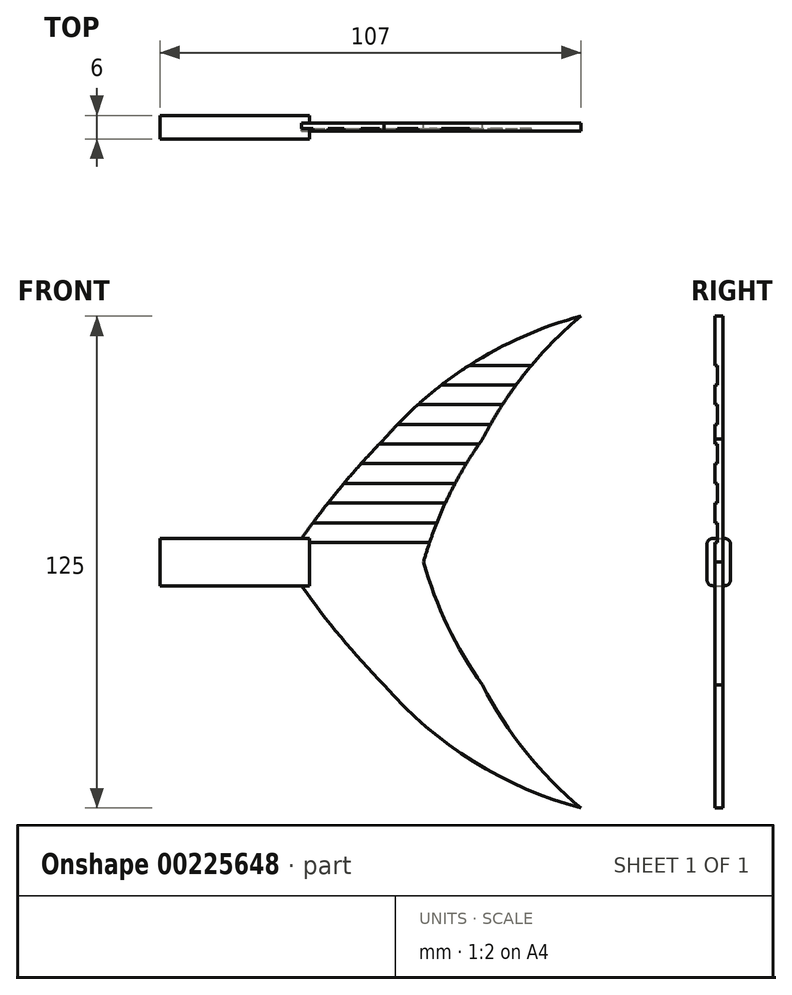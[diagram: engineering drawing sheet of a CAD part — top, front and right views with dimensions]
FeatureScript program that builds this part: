
annotation { "Feature Type Name" : "Feature", "Feature Type Description" : "" }
export const myFeature = defineFeature(function(context is Context, id is Id, definition is map)
    precondition{}
    {
        {
            var Q0;
            Q0=qCreatedBy(makeId("Front.planeOp"),FACE);
            var sketch = newSketch(context, id + "F0", { "sketchPlane" : qUnion([Q0])});
            skLineSegment(sketch, "E0", {"start": v(0, 0) * mm, "end": v(35, 0) * mm});
            skLineSegment(sketch, "E1", {"start": v(25, 31.25) * mm, "end": v(50, 31.25) * mm});
            skPoint(sketch, "E2", {"position": v(75, 62.5) * mm});
            skArc(sketch, "E3", {"start": v(25, 31.25) * mm, "mid": v(11.72, 16.25) * mm, "end": v(0, 0) * mm});
            skArc(sketch, "E4", {"start": v(75, 62.5) * mm, "mid": v(47.64, 50.64) * mm, "end": v(25, 31.25) * mm});
            skArc(sketch, "E5", {"start": v(75, 62.5) * mm, "mid": v(60.92, 48.14) * mm, "end": v(50, 31.25) * mm});
            skArc(sketch, "E6", {"start": v(50, 31.25) * mm, "mid": v(41.14, 16.28) * mm, "end": v(35, 0) * mm});
            skSolve(sketch);
        }
        {
            var Q0;
            Q0=qSketchRegion(id+"F0",true);
            extrude(context, id + "F1", {"entities" : qUnion([Q0]), "endBound" : BoundingType.SYMMETRIC, "depth" : 2 * mm});
        }
        {
            var Q0;
            Q0=makeQuery(id+"F1.opExtrude","SWEPT_BODY",BODY,{"disambiguationData":[OSD([sQuery(id+"F0.wireOp",EDGE,"E0"),sQuery(id+"F0.wireOp",EDGE,"E3"),sQuery(id+"F0.wireOp",EDGE,"E4"),sQuery(id+"F0.wireOp",EDGE,"E5"),sQuery(id+"F0.wireOp",EDGE,"E6")])]});
            var Q1;
            Q1=qCreatedBy(makeId("Top.planeOp"),FACE);
            mirror(context, id + "F2", {"operationType" : NewBodyOperationType.ADD, "entities" : qUnion([Q0]), "mirrorPlane" : qUnion([Q1])});
        }
        {
            var Q0;
            {var subQ0=makeQuery(id+"F1.opExtrude","CAP_FACE",FACE,{"disambiguationData":[OSD([sQuery(id+"F0.wireOp",EDGE,"E0"),sQuery(id+"F0.wireOp",EDGE,"E3"),sQuery(id+"F0.wireOp",EDGE,"E4"),sQuery(id+"F0.wireOp",EDGE,"E5"),sQuery(id+"F0.wireOp",EDGE,"E6")])],"isStart":false});Q0=makeQuery(id+"F2.boolean.opBoolean","MERGE",FACE,{"derivedFrom":[subQ0,makeQuery(id+"F2.opPattern","COPY",FACE,{"derivedFrom":subQ0,"instanceName":"1"})]});}
            var sketch = newSketch(context, id + "F3", { "sketchPlane" : qUnion([Q0])});
            skLineSegment(sketch, "E7.bottom", {"start": v(-1.98, 10) * mm, "end": v(47.03, 10) * mm});
            skLineSegment(sketch, "E7.top", {"start": v(-1.98, 5) * mm, "end": v(47.03, 5) * mm});
            skLineSegment(sketch, "E7.left", {"start": v(-1.98, 10) * mm, "end": v(-1.98, 5) * mm});
            skLineSegment(sketch, "E7.right", {"start": v(47.03, 10) * mm, "end": v(47.03, 5) * mm});
            skLineSegment(sketch, "E8.bottom", {"start": v(3.2, 20) * mm, "end": v(51.44, 20) * mm});
            skLineSegment(sketch, "E8.top", {"start": v(3.2, 15) * mm, "end": v(51.44, 15) * mm});
            skLineSegment(sketch, "E8.left", {"start": v(3.2, 20) * mm, "end": v(3.2, 15) * mm});
            skLineSegment(sketch, "E8.right", {"start": v(51.44, 20) * mm, "end": v(51.44, 15) * mm});
            skLineSegment(sketch, "E9.bottom", {"start": v(15.73, 30) * mm, "end": v(55.62, 30) * mm});
            skLineSegment(sketch, "E9.top", {"start": v(15.73, 25) * mm, "end": v(55.62, 25) * mm});
            skLineSegment(sketch, "E9.left", {"start": v(15.73, 30) * mm, "end": v(15.73, 25) * mm});
            skLineSegment(sketch, "E9.right", {"start": v(55.62, 30) * mm, "end": v(55.62, 25) * mm});
            skLineSegment(sketch, "E10.bottom", {"start": v(22.08, 40) * mm, "end": v(60.93, 40) * mm});
            skLineSegment(sketch, "E10.top", {"start": v(22.08, 35) * mm, "end": v(60.93, 35) * mm});
            skLineSegment(sketch, "E10.left", {"start": v(22.08, 40) * mm, "end": v(22.08, 35) * mm});
            skLineSegment(sketch, "E10.right", {"start": v(60.93, 40) * mm, "end": v(60.93, 35) * mm});
            skLineSegment(sketch, "E11.bottom", {"start": v(28.82, 50) * mm, "end": v(67.6, 50) * mm});
            skLineSegment(sketch, "E11.top", {"start": v(28.82, 45) * mm, "end": v(67.6, 45) * mm});
            skLineSegment(sketch, "E11.left", {"start": v(28.82, 50) * mm, "end": v(28.82, 45) * mm});
            skLineSegment(sketch, "E11.right", {"start": v(67.6, 50) * mm, "end": v(67.6, 45) * mm});
            skSolve(sketch);
        }
        {
            var Q0;
            {var subQ0=sQuery(id+"F3.wireOp",EDGE,"E11.bottom");var subQ1=sQuery(id+"F0.wireOp",EDGE,"E5");var subQ2=sQuery(id+"F0.wireOp",EDGE,"E4");var subQ3=makeQuery(id+"F1.opExtrude","CAP_FACE",FACE,{"disambiguationData":[OSD([sQuery(id+"F0.wireOp",EDGE,"E0"),sQuery(id+"F0.wireOp",EDGE,"E3"),subQ2,subQ1,sQuery(id+"F0.wireOp",EDGE,"E6")])],"isStart":false});var subQ4=makeQuery(id+"F2.boolean.opBoolean","MERGE",FACE,{"derivedFrom":[subQ3,makeQuery(id+"F2.opPattern","COPY",FACE,{"derivedFrom":subQ3,"instanceName":"1"})]});var subQ5=makeQuery(id+"FWRJaHnI6FiFIvM_1.opFillet","BLEND_EDGE",EDGE,{"blendedFrom":[makeQuery(id+"F1.opExtrude","CAP_EDGE",EDGE,{"disambiguationData":[OSD([subQ2])],"isStart":false}),subQ4],"blendedInto":[subQ4]});var subQ6=makeQuery(id+"F3.imprint","INTERSECT",VERTEX,{"derivedFrom":[subQ5,subQ0]});Q0=makeQuery(id+"F3.imprint","IMPRINT",FACE,{"disambiguationData":[TD([[makeQuery(id+"F3.imprint","IMPRINT",EDGE,{"disambiguationData":[TD([[subQ6,-1.0]])],"derivedFrom":subQ0}),-1.0]])]});}
            var Q1;
            {var subQ0=sQuery(id+"F3.wireOp",EDGE,"E10.bottom");var subQ1=sQuery(id+"F0.wireOp",EDGE,"E5");var subQ2=sQuery(id+"F0.wireOp",EDGE,"E4");var subQ3=makeQuery(id+"F1.opExtrude","CAP_FACE",FACE,{"disambiguationData":[OSD([sQuery(id+"F0.wireOp",EDGE,"E0"),sQuery(id+"F0.wireOp",EDGE,"E3"),subQ2,subQ1,sQuery(id+"F0.wireOp",EDGE,"E6")])],"isStart":false});var subQ4=makeQuery(id+"F2.boolean.opBoolean","MERGE",FACE,{"derivedFrom":[subQ3,makeQuery(id+"F2.opPattern","COPY",FACE,{"derivedFrom":subQ3,"instanceName":"1"})]});var subQ5=makeQuery(id+"FWRJaHnI6FiFIvM_1.opFillet","BLEND_EDGE",EDGE,{"blendedFrom":[makeQuery(id+"F1.opExtrude","CAP_EDGE",EDGE,{"disambiguationData":[OSD([subQ2])],"isStart":false}),subQ4],"blendedInto":[subQ4]});var subQ6=makeQuery(id+"F3.imprint","INTERSECT",VERTEX,{"derivedFrom":[subQ5,subQ0]});Q1=makeQuery(id+"F3.imprint","IMPRINT",FACE,{"disambiguationData":[TD([[makeQuery(id+"F3.imprint","IMPRINT",EDGE,{"disambiguationData":[TD([[subQ6,-1.0]])],"derivedFrom":subQ0}),-1.0]])]});}
            var Q2;
            {var subQ0=sQuery(id+"F3.wireOp",EDGE,"E9.bottom");var subQ1=sQuery(id+"F0.wireOp",EDGE,"E6");var subQ2=sQuery(id+"F0.wireOp",EDGE,"E3");var subQ3=makeQuery(id+"F1.opExtrude","CAP_FACE",FACE,{"disambiguationData":[OSD([sQuery(id+"F0.wireOp",EDGE,"E0"),subQ2,sQuery(id+"F0.wireOp",EDGE,"E4"),sQuery(id+"F0.wireOp",EDGE,"E5"),subQ1])],"isStart":false});var subQ4=makeQuery(id+"F2.boolean.opBoolean","MERGE",FACE,{"derivedFrom":[subQ3,makeQuery(id+"F2.opPattern","COPY",FACE,{"derivedFrom":subQ3,"instanceName":"1"})]});var subQ5=makeQuery(id+"FWRJaHnI6FiFIvM_1.opFillet","BLEND_EDGE",EDGE,{"blendedFrom":[makeQuery(id+"F1.opExtrude","CAP_EDGE",EDGE,{"disambiguationData":[OSD([subQ2])],"isStart":false}),subQ4],"blendedInto":[subQ4]});var subQ6=makeQuery(id+"F3.imprint","INTERSECT",VERTEX,{"derivedFrom":[subQ5,subQ0]});Q2=makeQuery(id+"F3.imprint","IMPRINT",FACE,{"disambiguationData":[TD([[makeQuery(id+"F3.imprint","IMPRINT",EDGE,{"disambiguationData":[TD([[subQ6,-1.0]])],"derivedFrom":subQ0}),-1.0]])]});}
            var Q3;
            {var subQ0=sQuery(id+"F3.wireOp",EDGE,"E7.bottom");var subQ1=sQuery(id+"F0.wireOp",EDGE,"E6");var subQ2=sQuery(id+"F0.wireOp",EDGE,"E3");var subQ3=makeQuery(id+"F1.opExtrude","CAP_FACE",FACE,{"disambiguationData":[OSD([sQuery(id+"F0.wireOp",EDGE,"E0"),subQ2,sQuery(id+"F0.wireOp",EDGE,"E4"),sQuery(id+"F0.wireOp",EDGE,"E5"),subQ1])],"isStart":false});var subQ4=makeQuery(id+"F2.boolean.opBoolean","MERGE",FACE,{"derivedFrom":[subQ3,makeQuery(id+"F2.opPattern","COPY",FACE,{"derivedFrom":subQ3,"instanceName":"1"})]});var subQ5=makeQuery(id+"FWRJaHnI6FiFIvM_1.opFillet","BLEND_EDGE",EDGE,{"blendedFrom":[makeQuery(id+"F1.opExtrude","CAP_EDGE",EDGE,{"disambiguationData":[OSD([subQ2])],"isStart":false}),subQ4],"blendedInto":[subQ4]});var subQ6=makeQuery(id+"F3.imprint","INTERSECT",VERTEX,{"derivedFrom":[subQ5,subQ0]});Q3=makeQuery(id+"F3.imprint","IMPRINT",FACE,{"disambiguationData":[TD([[makeQuery(id+"F3.imprint","IMPRINT",EDGE,{"disambiguationData":[TD([[subQ6,-1.0]])],"derivedFrom":subQ0}),-1.0]])]});}
            var Q4;
            {var subQ0=sQuery(id+"F3.wireOp",EDGE,"E8.bottom");var subQ1=sQuery(id+"F0.wireOp",EDGE,"E6");var subQ2=sQuery(id+"F0.wireOp",EDGE,"E3");var subQ3=makeQuery(id+"F1.opExtrude","CAP_FACE",FACE,{"disambiguationData":[OSD([sQuery(id+"F0.wireOp",EDGE,"E0"),subQ2,sQuery(id+"F0.wireOp",EDGE,"E4"),sQuery(id+"F0.wireOp",EDGE,"E5"),subQ1])],"isStart":false});var subQ4=makeQuery(id+"F2.boolean.opBoolean","MERGE",FACE,{"derivedFrom":[subQ3,makeQuery(id+"F2.opPattern","COPY",FACE,{"derivedFrom":subQ3,"instanceName":"1"})]});var subQ5=makeQuery(id+"FWRJaHnI6FiFIvM_1.opFillet","BLEND_EDGE",EDGE,{"blendedFrom":[makeQuery(id+"F1.opExtrude","CAP_EDGE",EDGE,{"disambiguationData":[OSD([subQ2])],"isStart":false}),subQ4],"blendedInto":[subQ4]});var subQ6=makeQuery(id+"F3.imprint","INTERSECT",VERTEX,{"derivedFrom":[subQ5,subQ0]});Q4=makeQuery(id+"F3.imprint","IMPRINT",FACE,{"disambiguationData":[TD([[makeQuery(id+"F3.imprint","IMPRINT",EDGE,{"disambiguationData":[TD([[subQ6,-1.0]])],"derivedFrom":subQ0}),-1.0]])]});}
            extrude(context, id + "F4", {"entities" : qUnion([Q0, Q1, Q2, Q3, Q4]), "operationType" : NewBodyOperationType.REMOVE, "oppositeDirection" : true, "depth" : 0.7 * mm});
        }
        {
            var Q0;
            Q0=qCreatedBy(makeId("Front.planeOp"),FACE);
            var sketch = newSketch(context, id + "F5", { "sketchPlane" : qUnion([Q0])});
            skLineSegment(sketch, "E12.bottom", {"start": v(6, 6) * mm, "end": v(-32, 6) * mm});
            skLineSegment(sketch, "E12.top", {"start": v(6, -6) * mm, "end": v(-32, -6) * mm});
            skLineSegment(sketch, "E12.left", {"start": v(6, 6) * mm, "end": v(6, -6) * mm});
            skLineSegment(sketch, "E12.right", {"start": v(-32, 6) * mm, "end": v(-32, -6) * mm});
            skSolve(sketch);
        }
        {
            var Q0;
            Q0=makeQuery(id+"F5.imprint","IMPRINT",FACE,{"disambiguationData":[TD([[makeQuery(id+"F5.imprint","IMPRINT",EDGE,{"derivedFrom":sQuery(id+"F5.wireOp",EDGE,"E12.bottom")}),1.0]])]});
            extrude(context, id + "F6", {"entities" : qUnion([Q0]), "operationType" : NewBodyOperationType.ADD, "endBound" : BoundingType.SYMMETRIC, "depth" : 6 * mm});
        }
        {
            var Q0;
            Q0=makeQuery(id+"F6.opExtrude","CAP_EDGE",EDGE,{"disambiguationData":[OSD([sQuery(id+"F5.wireOp",EDGE,"E12.bottom")])],"isStart":true});
            var Q1;
            Q1=makeQuery(id+"F6.opExtrude","CAP_EDGE",EDGE,{"disambiguationData":[OSD([sQuery(id+"F5.wireOp",EDGE,"E12.bottom")])],"isStart":false});
            var Q2;
            Q2=makeQuery(id+"F6.opExtrude","CAP_EDGE",EDGE,{"disambiguationData":[OSD([sQuery(id+"F5.wireOp",EDGE,"E12.top")])],"isStart":false});
            var Q3;
            Q3=makeQuery(id+"F6.opExtrude","CAP_EDGE",EDGE,{"disambiguationData":[OSD([sQuery(id+"F5.wireOp",EDGE,"E12.top")])],"isStart":true});
            fillet(context, id + "F7", {"entities" : qUnion([Q0, Q1, Q2, Q3]), "radius" : 1.5 * mm, "tangentPropagation" : true, "allowEdgeOverflow" : false});
        }
    });
